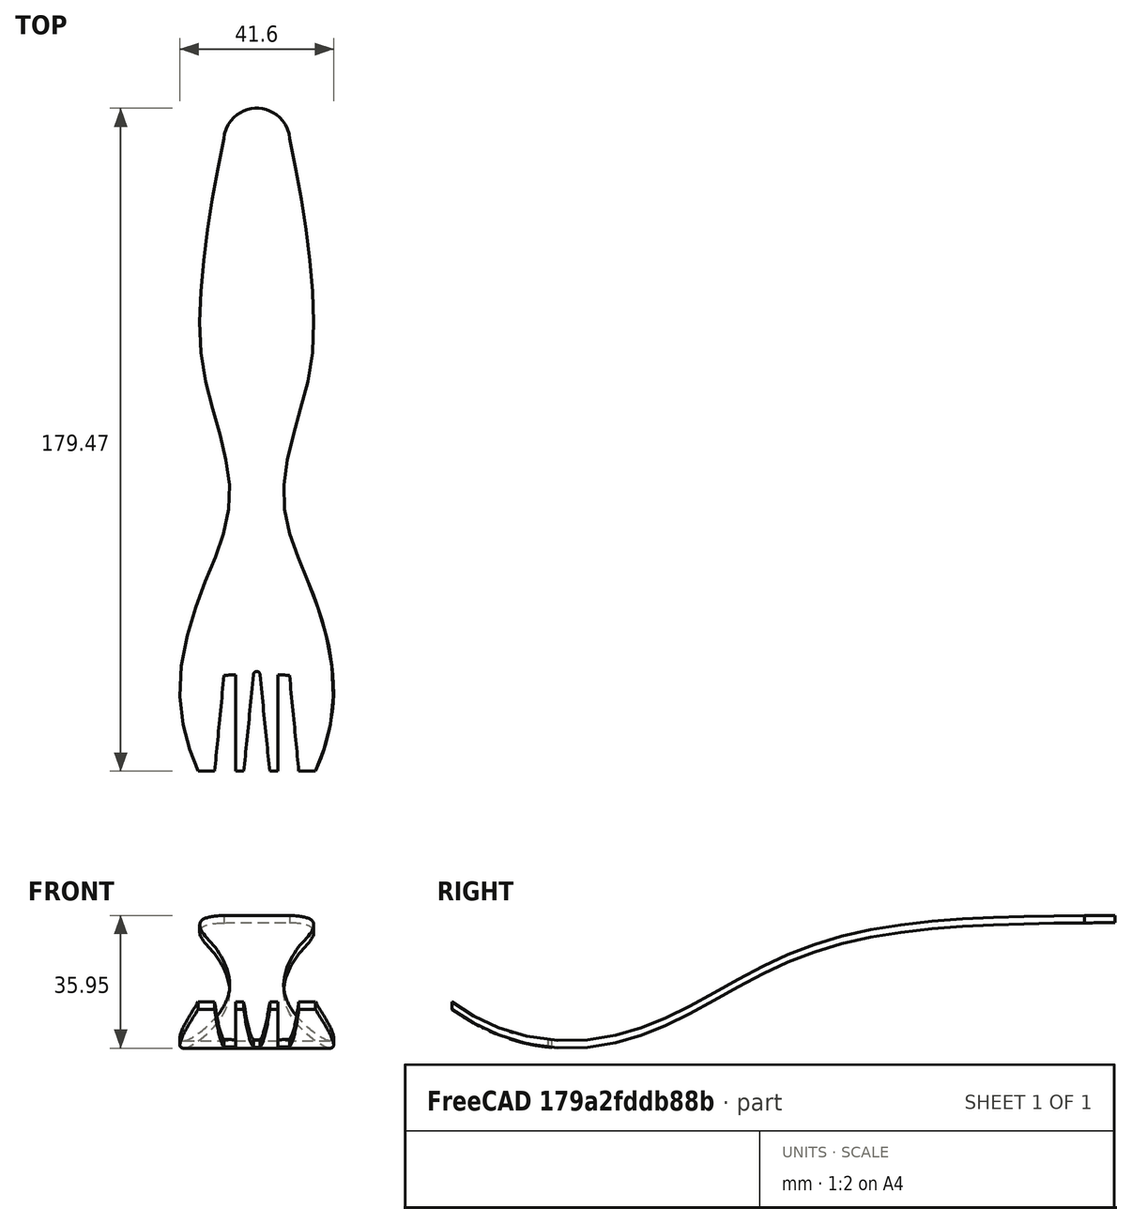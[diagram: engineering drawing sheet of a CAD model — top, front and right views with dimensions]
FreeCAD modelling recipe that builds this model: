
FCSTD DOCUMENT  (FreeCAD 0.20R29177 +426 (Git))
Label: proj_17
License: All rights reserved
LicenseURL: http://en.wikipedia.org/wiki/All_rights_reserved
objects: Part::Extrusion×3, Sketcher::SketchObject×2, Part::MultiCommon×1
note: 6 computed .brp shape members not serialized (recipe doc carries the construction recipe); baked Part::Feature solids carry a one-line shape summary decoded from their .brp

FEATURE [Sketcher::SketchObject] Sketch
  FullyConstrained = false
  Placement = pos=(0,0,0) rot=(0.57735,0.57735,0.57735;2.0944rad)
  sketch-geometry (13):
    g0-g6: Circle x7 (B-spline internal-alignment scaffolding for g7; pole/knot coordinates omitted)
    g7: BSplineCurve PolesCount=7 KnotsCount=5 Degree=3 IsPeriodic=0
    g8-g12: GeomPoint x5 (B-spline internal-alignment scaffolding for g7; pole/knot coordinates omitted)
  constraints (4):
    c: Weight(g0) = 1
    c: Equal(g0, g1-g6) x6
    c: InternalAlignment(g0-g6 -> g7) x7
    c: InternalAlignment(g8-g12 -> g7) x5
FEATURE [Part::Extrusion] Extrude
  Base = -> Sketch
  Dir = (0,0,1)
  DirMode = 0
  FaceMakerClass = Part::FaceMakerBullseye
  LengthFwd = 2
  LengthRev = 0
  Solid = false
  Symmetric = false
FEATURE [Part::Extrusion] Extrude001
  Base = -> Extrude
  Dir = (1,0,0)
  DirMode = 0
  FaceMakerClass = Part::FaceMakerBullseye
  LengthFwd = 60
  LengthRev = 0
  Solid = false
  Symmetric = true
FEATURE [Sketcher::SketchObject] Sketch001
  FullyConstrained = false
  Placement = pos=(0,0,40) rot=(0,0,1;0rad)
  sketch-geometry (45):
    g0: LineSegment StartX=48.0309 StartY=51.7993 StartZ=0 EndX=-49.5472 EndY=51.7993 EndZ=0
    g1-g8: Circle x8 (B-spline internal-alignment scaffolding for g9; pole/knot coordinates omitted)
    g9: BSplineCurve PolesCount=8 KnotsCount=6 Degree=3 IsPeriodic=0
    g10-g15: GeomPoint x6 (B-spline internal-alignment scaffolding for g9; pole/knot coordinates omitted)
    g16: LineSegment StartX=-15.8906 StartY=-34.2672 StartZ=0 EndX=-11.3839 EndY=-34.2672 EndZ=0
    g17: LineSegment StartX=-11.3839 StartY=-34.2672 StartZ=0 EndX=-8.86031 EndY=-8.38627 EndZ=0
    g18: LineSegment StartX=-8.86031 StartY=-8.38626 StartZ=0 EndX=-5.74296 EndY=-8.23782 EndZ=0
    g19: LineSegment StartX=-5.74296 StartY=-8.23782 StartZ=0 EndX=-5.74296 EndY=-34.3642 EndZ=0
    g20: LineSegment StartX=-5.74296 StartY=-34.3642 StartZ=0 EndX=-3.51627 EndY=-34.3642 EndZ=0
    g21: LineSegment StartX=-0.866711 StartY=-8.23308 StartZ=0 EndX=-3.51627 EndY=-34.3642 EndZ=0
    g22-g29: Circle x8 (B-spline internal-alignment scaffolding for g30; pole/knot coordinates omitted)
    g30: BSplineCurve PolesCount=8 KnotsCount=6 Degree=3 IsPeriodic=0
    g31-g36: GeomPoint x6 (B-spline internal-alignment scaffolding for g30; pole/knot coordinates omitted)
    g37: LineSegment StartX=15.8906 StartY=-34.2672 StartZ=0 EndX=11.3839 EndY=-34.2672 EndZ=0
    g38: LineSegment StartX=11.3839 StartY=-34.2672 StartZ=0 EndX=8.86031 EndY=-8.38627 EndZ=0
    g39: LineSegment StartX=8.86031 StartY=-8.38626 StartZ=0 EndX=5.74296 EndY=-8.23782 EndZ=0
    g40: LineSegment StartX=5.74296 StartY=-8.23782 StartZ=0 EndX=5.74296 EndY=-34.3642 EndZ=0
    g41: LineSegment StartX=5.74296 StartY=-34.3642 StartZ=0 EndX=3.51627 EndY=-34.3642 EndZ=0
    g42: LineSegment StartX=0.866711 StartY=-8.23308 StartZ=0 EndX=3.51627 EndY=-34.3642 EndZ=0
    g43: ArcOfCircle CenterX=0 CenterY=-8.18333 CenterZ=0 NormalX=0 NormalY=0 NormalZ=1 AngleXU=0 Radius=0.868138 StartAngle=6.22585 EndAngle=9.48211
    g44: ArcOfCircle CenterX=0 CenterY=136.155 CenterZ=0 NormalX=0 NormalY=0 NormalZ=1 AngleXU=0 Radius=8.95406 StartAngle=0.0761327 EndAngle=3.06546
  constraints (39):
    c: Horizontal(g0)
    c: Weight(g1) = 1
    c: Equal(g1, g2-g8) x7
    c: InternalAlignment(g1-g8 -> g9) x8
    c: InternalAlignment(g10-g15 -> g9) x6
    c: Coincident(g16,g9)
    c: Horizontal(g16)
    c: Coincident(g17,g16)
    c: Coincident(g18,g17)
    c: Coincident(g19,g18)
    c: Vertical(g19)
    c: Coincident(g20,g19)
    c: Horizontal(g20)
    c: Coincident(g21,g20)
    c: Weight(g22) = 1
    c: Equal(g22, g23-g29) x7
    c: InternalAlignment(g22-g29 -> g30) x8
    c: InternalAlignment(g31-g36 -> g30) x6
    c: Coincident(g37,g30)
    c: Horizontal(g37)
    c: Coincident(g38,g37)
    c: Coincident(g39,g38)
    c: Coincident(g40,g39)
    c: Vertical(g40)
    c: Coincident(g41,g40)
    c: Horizontal(g41)
    c: Coincident(g42,g41)
    c: Horizontal(g25,g4)
    c: Horizontal(g26,g5)
    c: Horizontal(g24,g3)
    c: Horizontal(g2,g23)
    c: Horizontal(g30,g9)
    c: Horizontal(g42,g21)
    c: Coincident(g43,g21)
    c: Coincident(g43,g42)
    c: Tangent(g43,g-2) = -1.5708
    c: Coincident(g44,g9)
    c: Coincident(g44,g30)
    c: PointOnObject(g44,g-2)
FEATURE [Part::Extrusion] Extrude002
  Base = -> Sketch001
  Dir = (0,0,1)
  DirMode = 2
  FaceMakerClass = Part::FaceMakerBullseye
  LengthFwd = 100
  LengthRev = 0
  Reversed = true
  Solid = true
  Symmetric = false
FEATURE [Part::MultiCommon] Common
  Shapes = -> [Extrude001,Extrude002]
